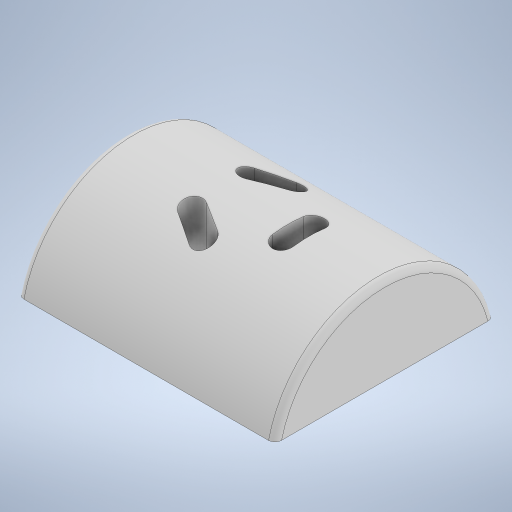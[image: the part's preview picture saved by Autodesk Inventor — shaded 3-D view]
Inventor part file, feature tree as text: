
AUTODESK INVENTOR PART (.ipt)
format: ipt  version: 2024.2 (Build 282272000, 272)  size: 314,880 bytes
history: native  units: mm
features: extrude x3, other x1, sketch x1, revolve x1, fillet x1
ambient origin geometry x8: Origin, YZ Plane, XZ Plane, XY Plane, X Axis, Y Axis, Z Axis, Center Point
bodies: Body1 (feature_tree)
feature tree (7):
  other  "Bryła1"
  sketch  "Szkic1"
  revolve  "Obrót2"
  extrude  "Wyciągnięcie proste1"  Depth=28.2mm
  extrude  "Wyciągnięcie proste2"  Depth=3.5mm
  extrude  "Wyciągnięcie proste3"  Depth=6.981317mm
  fillet  "Zaokrąglenie1"  Radius=30.0mm
